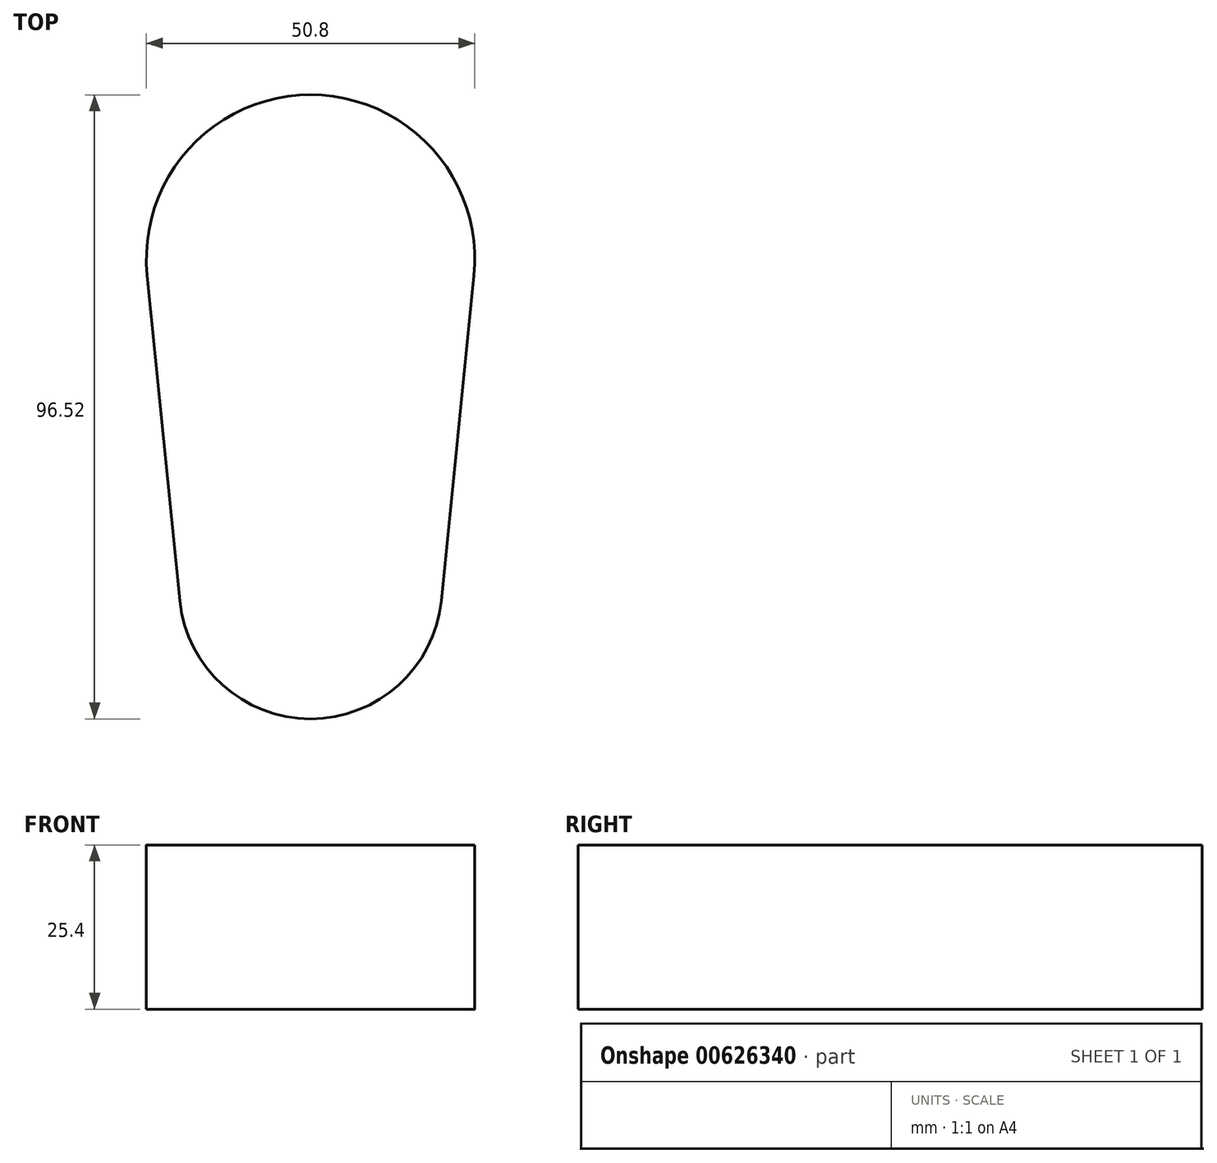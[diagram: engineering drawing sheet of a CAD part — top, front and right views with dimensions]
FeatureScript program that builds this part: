
annotation { "Feature Type Name" : "Feature", "Feature Type Description" : "" }
export const myFeature = defineFeature(function(context is Context, id is Id, definition is map)
    precondition{}
    {
        {
            var Q0;
            Q0=qCreatedBy(makeId("Top.planeOp"),FACE);
            var sketch = newSketch(context, id + "F0", { "sketchPlane" : qUnion([Q0])});
            skLineSegment(sketch, "E0", {"start": v(20.22, -2.03) * mm, "end": v(25.27, 48.26) * mm});
            skArc(sketch, "E1", {"start": v(25.27, 48.26) * mm, "mid": v(0, 76.2) * mm, "end": v(-25.27, 48.26) * mm});
            skLineSegment(sketch, "E2", {"start": v(-25.27, 48.26) * mm, "end": v(-20.22, -2.03) * mm});
            skArc(sketch, "E3", {"start": v(-20.22, -2.03) * mm, "mid": v(0, -20.32) * mm, "end": v(20.22, -2.03) * mm});
            skSolve(sketch);
        }
        {
            var Q0;
            Q0=qSketchRegion(id+"F0",true);
            extrude(context, id + "F1", {"entities" : qUnion([Q0]), "depth" : 25.4 * mm, "offsetDistance" : 25.4 * mm});
        }
    });
